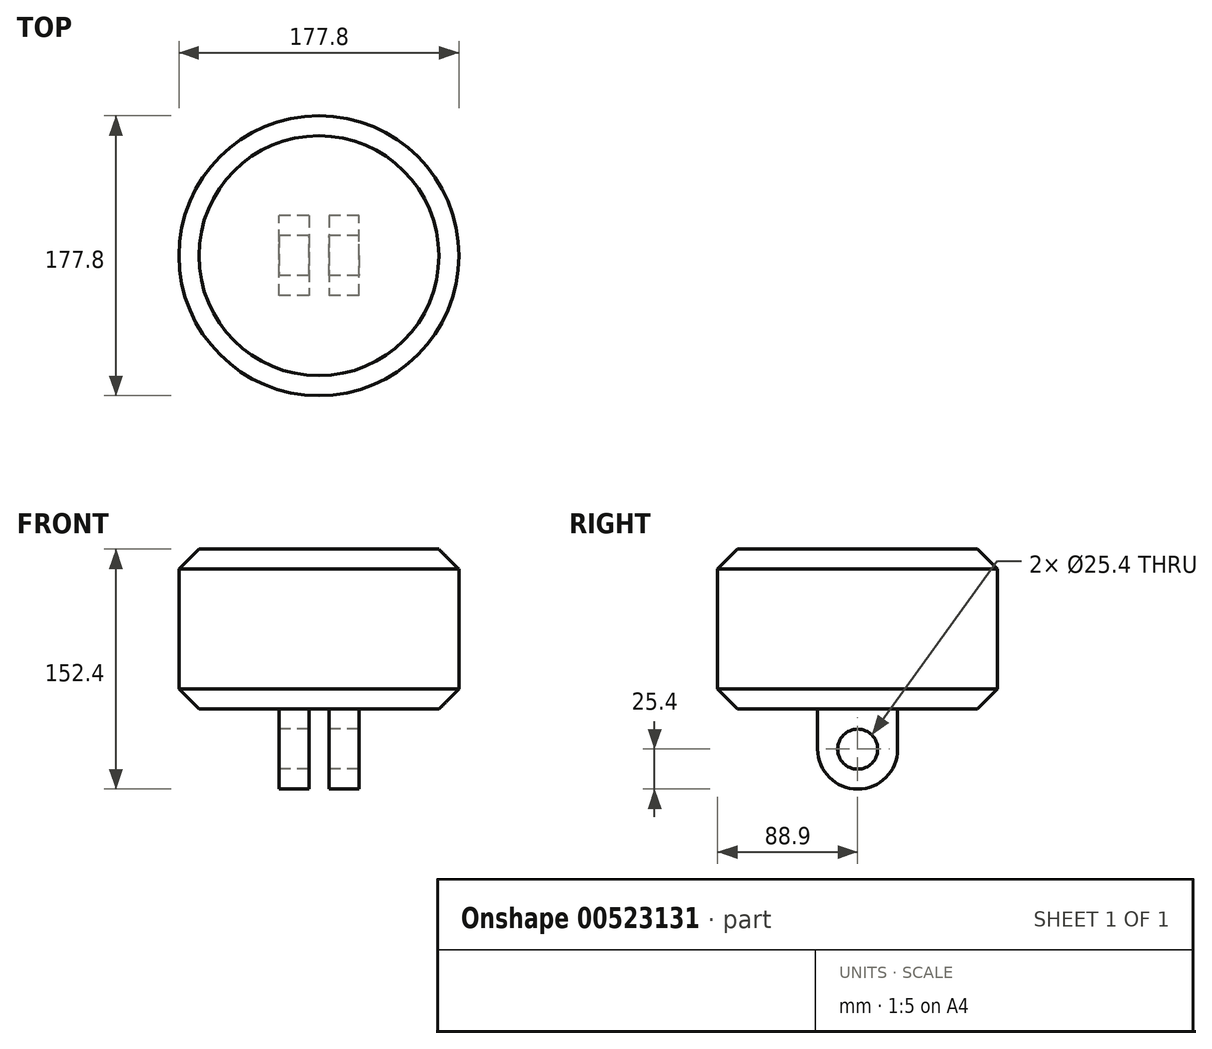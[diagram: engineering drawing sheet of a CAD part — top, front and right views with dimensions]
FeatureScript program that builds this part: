
annotation { "Feature Type Name" : "Feature", "Feature Type Description" : "" }
export const myFeature = defineFeature(function(context is Context, id is Id, definition is map)
    precondition{}
    {
        {
            var Q0;
            Q0=qCreatedBy(makeId("Top.planeOp"),FACE);
            var sketch = newSketch(context, id + "F0", { "sketchPlane" : qUnion([Q0])});
            skCircle(sketch, "E0", {"center": v(0, 0) * mm, "radius": 88.9 * mm});
            skSolve(sketch);
        }
        {
            var Q0;
            Q0 = qSketchRegion(id + "F0", true);
            extrude(context, id + "F1", {"entities" : qUnion([Q0]), "depth" : 101.6 * mm, "offsetDistance" : 25.4 * mm});
        }
        {
            var Q0;
            Q0=makeQuery(id+"F1.opExtrude","CAP_EDGE",EDGE,{"disambiguationData":[OSD([sQuery(id+"F0.wireOp",EDGE,"E0")])],"isStart":false});
            var Q1;
            Q1=makeQuery(id+"F1.opExtrude","CAP_EDGE",EDGE,{"disambiguationData":[OSD([sQuery(id+"F0.wireOp",EDGE,"E0")])],"isStart":true});
            chamfer(context, id + "F2", {"entities" : qUnion([Q0, Q1]), "width" : 12.7 * mm, "tangentPropagation" : true});
        }
        {
            var Q0;
            Q0=makeQuery(id+"F1.opExtrude","CAP_FACE",FACE,{"disambiguationData":[OSD([sQuery(id+"F0.wireOp",EDGE,"E0")])],"isStart":true});
            var sketch = newSketch(context, id + "F3", { "sketchPlane" : qUnion([Q0])});
            skLineSegment(sketch, "E1.bottom", {"start": v(25.4, 25.4) * mm, "end": v(-25.4, 25.4) * mm});
            skLineSegment(sketch, "E1.top", {"start": v(25.4, -25.4) * mm, "end": v(-25.4, -25.4) * mm});
            skLineSegment(sketch, "E1.left", {"start": v(25.4, 25.4) * mm, "end": v(25.4, -25.4) * mm});
            skLineSegment(sketch, "E1.right", {"start": v(-25.4, 25.4) * mm, "end": v(-25.4, -25.4) * mm});
            skPoint(sketch, "E1.middle", {"position": v(0, 0) * mm});
            skSolve(sketch);
        }
        {
            var Q0;
            Q0 = qSketchRegion(id + "F3", true);
            extrude(context, id + "F4", {"entities" : qUnion([Q0]), "operationType" : NewBodyOperationType.ADD, "depth" : 50.8 * mm, "offsetDistance" : 25.4 * mm});
        }
        {
            var Q0;
            Q0=makeQuery(id+"F4.opExtrude","SWEPT_FACE",FACE,{"disambiguationData":[OSD([sQuery(id+"F3.wireOp",EDGE,"E1.bottom")])]});
            var sketch = newSketch(context, id + "F5", { "sketchPlane" : qUnion([Q0])});
            skLineSegment(sketch, "E2.bottom", {"start": v(6.35, 0) * mm, "end": v(-6.35, 0) * mm});
            skLineSegment(sketch, "E2.top", {"start": v(6.35, -50.8) * mm, "end": v(-6.35, -50.8) * mm});
            skLineSegment(sketch, "E2.left", {"start": v(6.35, 0) * mm, "end": v(6.35, -50.8) * mm});
            skLineSegment(sketch, "E2.right", {"start": v(-6.35, 0) * mm, "end": v(-6.35, -50.8) * mm});
            skPoint(sketch, "E2.middle", {"position": v(0, -25.4) * mm});
            skPoint(sketch, "E2.middle.positionSnap0", {"position": v(25.4, -25.4) * mm});
            skPoint(sketch, "E2.centerSnap0", {"position": v(25.4, -25.4) * mm});
            skSolve(sketch);
        }
        {
            var Q0;
            Q0 = qSketchRegion(id + "F5", true);
            extrude(context, id + "F6", {"entities" : qUnion([Q0]), "operationType" : NewBodyOperationType.REMOVE, "oppositeDirection" : true, "depth" : 50.8 * mm, "offsetDistance" : 25.4 * mm});
        }
        {
            var Q0;
            {var subQ0=sQuery(id+"F3.wireOp",EDGE,"E1.bottom");var subQ1=sQuery(id+"F3.wireOp",EDGE,"E1.right");Q0=makeQuery(id+"F6.boolean.opBoolean","SPLIT",EDGE,{"disambiguationData":[TD([makeQuery(id+"F4.opExtrude","SWEPT_FACE",FACE,{"disambiguationData":[OSD([subQ1])]})])],"derivedFrom":makeQuery(id+"F4.opExtrude","CAP_EDGE",EDGE,{"disambiguationData":[OSD([subQ0])],"isStart":false})});}
            var Q1;
            {var subQ0=sQuery(id+"F3.wireOp",EDGE,"E1.right");var subQ1=sQuery(id+"F3.wireOp",EDGE,"E1.top");Q1=makeQuery(id+"F6.boolean.opBoolean","SPLIT",EDGE,{"disambiguationData":[TD([makeQuery(id+"F4.opExtrude","SWEPT_FACE",FACE,{"disambiguationData":[OSD([subQ0])]})])],"derivedFrom":makeQuery(id+"F4.opExtrude","CAP_EDGE",EDGE,{"disambiguationData":[OSD([subQ1])],"isStart":false})});}
            var Q2;
            {var subQ0=sQuery(id+"F3.wireOp",EDGE,"E1.left");var subQ1=sQuery(id+"F3.wireOp",EDGE,"E1.top");Q2=makeQuery(id+"F6.boolean.opBoolean","SPLIT",EDGE,{"disambiguationData":[TD([makeQuery(id+"F4.opExtrude","SWEPT_FACE",FACE,{"disambiguationData":[OSD([subQ0])]})])],"derivedFrom":makeQuery(id+"F4.opExtrude","CAP_EDGE",EDGE,{"disambiguationData":[OSD([subQ1])],"isStart":false})});}
            var Q3;
            {var subQ0=sQuery(id+"F3.wireOp",EDGE,"E1.bottom");var subQ1=sQuery(id+"F3.wireOp",EDGE,"E1.left");Q3=makeQuery(id+"F6.boolean.opBoolean","SPLIT",EDGE,{"disambiguationData":[TD([makeQuery(id+"F4.opExtrude","SWEPT_FACE",FACE,{"disambiguationData":[OSD([subQ1])]})])],"derivedFrom":makeQuery(id+"F4.opExtrude","CAP_EDGE",EDGE,{"disambiguationData":[OSD([subQ0])],"isStart":false})});}
            fillet(context, id + "F7", {"entities" : qUnion([Q0, Q1, Q2, Q3]), "radius" : 25.4 * mm, "tangentPropagation" : true, "allowEdgeOverflow" : false});
        }
        {
            var Q0;
            Q0=makeQuery(id+"F4.opExtrude","SWEPT_FACE",FACE,{"disambiguationData":[OSD([sQuery(id+"F3.wireOp",EDGE,"E1.right")])]});
            var sketch = newSketch(context, id + "F8", { "sketchPlane" : qUnion([Q0])});
            skCircle(sketch, "E3", {"center": v(0, -25.4) * mm, "radius": 12.7 * mm});
            skSolve(sketch);
        }
        {
            var Q0;
            Q0 = qSketchRegion(id + "F8", true);
            var Q1;
            Q1=makeQuery(id+"F4.opExtrude","SWEPT_FACE",FACE,{"disambiguationData":[OSD([sQuery(id+"F3.wireOp",EDGE,"E1.left")])]});
            extrude(context, id + "F9", {"entities" : qUnion([Q0]), "operationType" : NewBodyOperationType.REMOVE, "endBound" : BoundingType.UP_TO_SURFACE, "oppositeDirection" : true, "depth" : 25.4 * mm, "endBoundEntityFace" : qUnion([Q1]), "offsetDistance" : 25.4 * mm});
        }
    });
